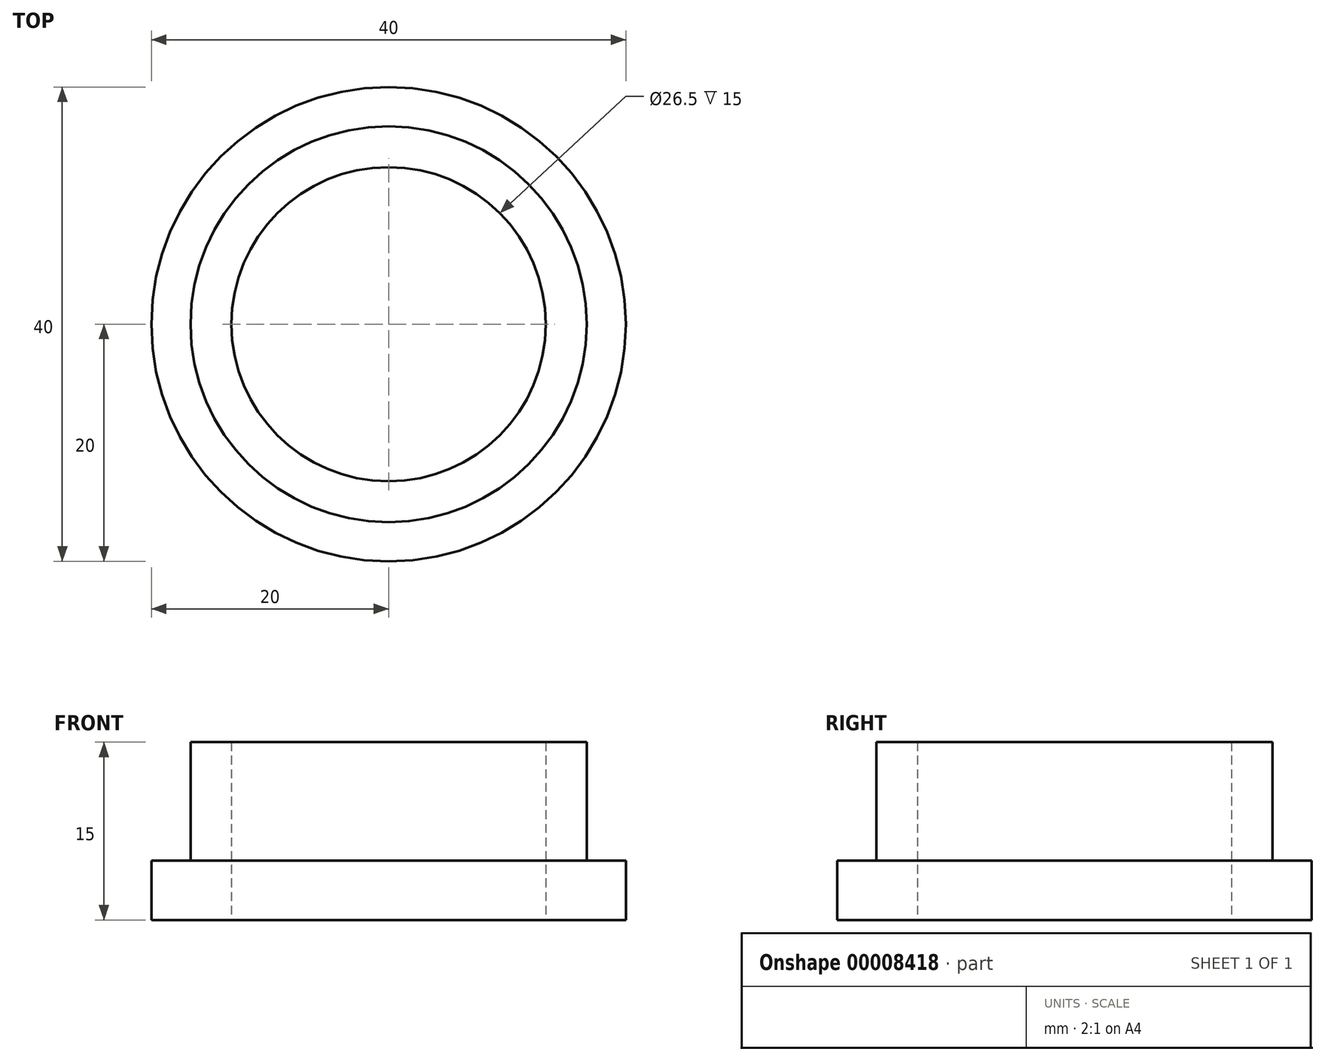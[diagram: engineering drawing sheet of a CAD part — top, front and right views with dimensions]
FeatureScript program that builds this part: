
annotation { "Feature Type Name" : "Feature", "Feature Type Description" : "" }
export const myFeature = defineFeature(function(context is Context, id is Id, definition is map)
    precondition{}
    {
        {
            var Q0;
            Q0=qCreatedBy(makeId("Top.planeOp"),FACE);
            var sketch = newSketch(context, id + "F0", { "sketchPlane" : qUnion([Q0])});
            skCircle(sketch, "E0", {"center": v(0, 0) * mm, "radius": 13.25 * mm});
            skCircle(sketch, "E1", {"center": v(0, 0) * mm, "radius": 16.7 * mm});
            skCircle(sketch, "E2", {"center": v(0, 0) * mm, "radius": 20 * mm});
            skSolve(sketch);
        }
        {
            var Q0;
            Q0 = qSketchRegion(id + "F0", true);
            extrude(context, id + "F1", {"entities" : qUnion([Q0]), "depth" : 5 * mm});
        }
        {
            var Q0;
            Q0=makeQuery(id+"F0.imprint","IMPRINT",FACE,{"disambiguationData":[TD([[makeQuery(id+"F0.imprint","IMPRINT",EDGE,{"derivedFrom":sQuery(id+"F0.wireOp",EDGE,"E0")}),-1.0]])]});
            extrude(context, id + "F2", {"entities" : qUnion([Q0]), "operationType" : NewBodyOperationType.ADD, "depth" : 15 * mm});
        }
    });
